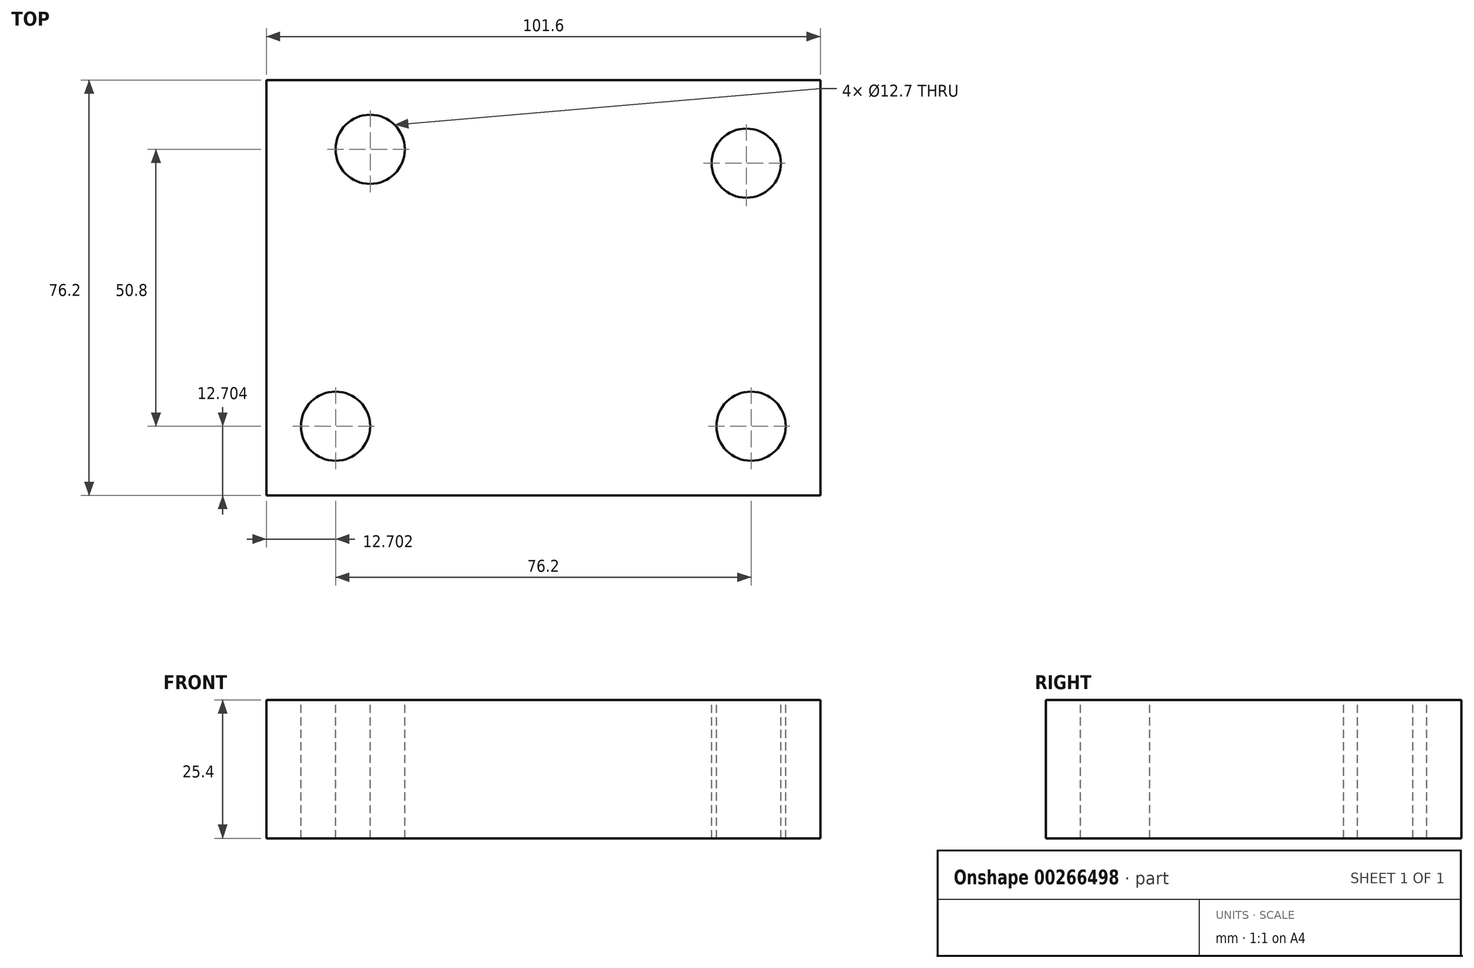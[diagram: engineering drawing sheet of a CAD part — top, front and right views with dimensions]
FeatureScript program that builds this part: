
annotation { "Feature Type Name" : "Feature", "Feature Type Description" : "" }
export const myFeature = defineFeature(function(context is Context, id is Id, definition is map)
    precondition{}
    {
        {
            var Q0;
            Q0=qCreatedBy(makeId("Top.planeOp"),FACE);
            var sketch = newSketch(context, id + "F0", { "sketchPlane" : qUnion([Q0])});
            skLineSegment(sketch, "E0.bottom", {"start": v(19.66, 38.36) * mm, "end": v(-81.94, 38.36) * mm});
            skLineSegment(sketch, "E0.top", {"start": v(19.66, -37.84) * mm, "end": v(-81.94, -37.84) * mm});
            skLineSegment(sketch, "E0.left", {"start": v(19.66, 38.36) * mm, "end": v(19.66, -37.84) * mm});
            skLineSegment(sketch, "E0.right", {"start": v(-81.94, 38.36) * mm, "end": v(-81.94, -37.84) * mm});
            skPoint(sketch, "E0.middle", {"position": v(-31.14, 0.26) * mm});
            skSolve(sketch);
        }
        {
            var Q0;
            Q0=makeQuery(id+"F0.imprint","IMPRINT",FACE,{"disambiguationData":[TD([[makeQuery(id+"F0.imprint","IMPRINT",EDGE,{"derivedFrom":sQuery(id+"F0.wireOp",EDGE,"E0.bottom")}),1.0]])]});
            extrude(context, id + "F1", {"entities" : qUnion([Q0]), "depth" : 25.4 * mm});
        }
        {
            var Q0;
            Q0=makeQuery(id+"F1.opExtrude","CAP_FACE",FACE,{"disambiguationData":[OSD([sQuery(id+"F0.wireOp",EDGE,"E0.bottom"),sQuery(id+"F0.wireOp",EDGE,"E0.top"),sQuery(id+"F0.wireOp",EDGE,"E0.left"),sQuery(id+"F0.wireOp",EDGE,"E0.right")])],"isStart":false});
            var sketch = newSketch(context, id + "F2", { "sketchPlane" : qUnion([Q0])});
            skCircle(sketch, "E1", {"center": v(-62.89, 25.66) * mm, "radius": 6.35 * mm});
            skCircle(sketch, "E2", {"center": v(-69.24, -25.14) * mm, "radius": 6.35 * mm});
            skCircle(sketch, "E3", {"center": v(6.08, 23.12) * mm, "radius": 6.35 * mm});
            skCircle(sketch, "E4", {"center": v(6.96, -25.14) * mm, "radius": 6.35 * mm});
            skSolve(sketch);
        }
        {
            var Q0;
            Q0=makeQuery(id+"F2.imprint","IMPRINT",FACE,{"disambiguationData":[TD([[makeQuery(id+"F2.imprint","IMPRINT",EDGE,{"derivedFrom":sQuery(id+"F2.wireOp",EDGE,"E1")}),1.0]])]});
            var Q1;
            Q1=makeQuery(id+"F2.imprint","IMPRINT",FACE,{"disambiguationData":[TD([[makeQuery(id+"F2.imprint","IMPRINT",EDGE,{"derivedFrom":sQuery(id+"F2.wireOp",EDGE,"E2")}),1.0]])]});
            var Q2;
            Q2=makeQuery(id+"F2.imprint","IMPRINT",FACE,{"disambiguationData":[TD([[makeQuery(id+"F2.imprint","IMPRINT",EDGE,{"derivedFrom":sQuery(id+"F2.wireOp",EDGE,"E4")}),1.0]])]});
            var Q3;
            Q3=makeQuery(id+"F2.imprint","IMPRINT",FACE,{"disambiguationData":[TD([[makeQuery(id+"F2.imprint","IMPRINT",EDGE,{"derivedFrom":sQuery(id+"F2.wireOp",EDGE,"E3")}),1.0]])]});
            extrude(context, id + "F3", {"entities" : qUnion([Q0, Q1, Q2, Q3]), "operationType" : NewBodyOperationType.REMOVE, "oppositeDirection" : true, "depth" : 25.4 * mm});
        }
    });
